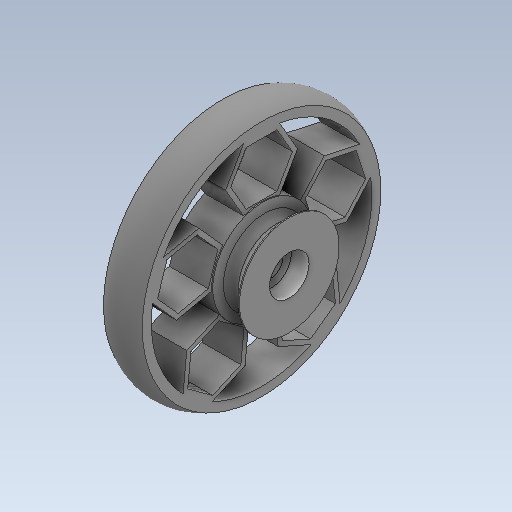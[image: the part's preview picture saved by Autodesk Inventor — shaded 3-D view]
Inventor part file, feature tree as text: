
AUTODESK INVENTOR PART (.ipt)
format: ipt  version: 2020 (Build 240168000, 168)  size: 318,976 bytes
history: native  units: in
note: dims shown in document units (in); Inventor stores cm internally (conversion verified against a paired STEP export)
features: sketch x4, other x3, extrude x3, revolve x1, projected_geometry x1
ambient origin geometry x8: Origin, YZ Plane, XZ Plane, XY Plane, X Axis, Y Axis, Z Axis, Center Point
bodies: Solid1 (feature_tree)
feature tree (12):
  other  "PulleyedWheelV1.ipt"
  extrude  "Extrusion1"  Depth=0.2756in
  extrude  "Extrusion2"  Depth=0.126in
  extrude  "Extrusion3"  Depth=0.126in
  revolve  "Revolution1"  [1 undecoded]
  other  "Solid1::PulleyedWheelV1.ipt"
  other  "TaggingFeature1"
  sketch  "Sketch1"  dims[d0=0.3937in]
  sketch  "Sketch2"  dims[d1=0.0394in d3=1.6929in d4=0.1181in d6=0.7087in d7=0.1969in d8=0.0in d9=1.6929in d10=0.063in d11=0.0315in d16=0.2756in d17=0.0in d20=0.0984in d24=0.0394in d26=45.0deg d2=0.2815in]
  sketch  "Sketch3"  dims[d5=0.126in d13=0.0in d15=0.2815in]
  sketch  "Sketch4"  dims[d18=0.126in d19=0.0in d21=0.1575in d23=0.0in d25=0.0in d28=45.0deg d29=90.0deg]
  projected_geometry  "Projected Loop1"
note: 1 required parameter value undecoded (feature->parameter linkage not recoverable at this tier; creation-order binding heuristic only, values carry confidence <= 0.55)
